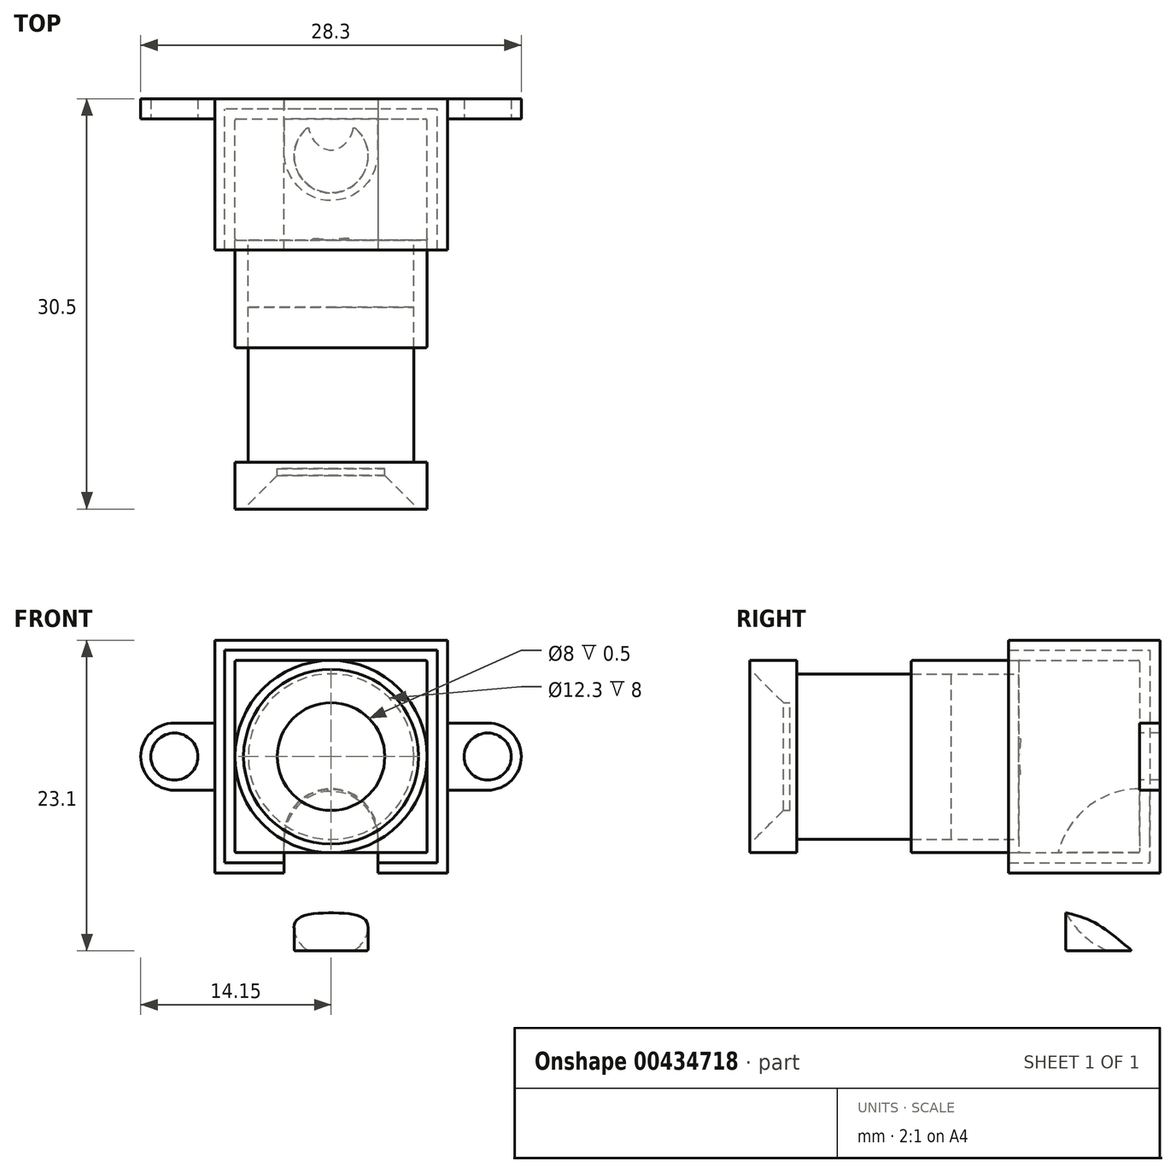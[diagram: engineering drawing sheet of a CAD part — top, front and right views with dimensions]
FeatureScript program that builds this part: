
annotation { "Feature Type Name" : "Feature", "Feature Type Description" : "" }
export const myFeature = defineFeature(function(context is Context, id is Id, definition is map)
    precondition{}
    {
        {
            var Q0;
            Q0=qCreatedBy(makeId("Front.planeOp"),FACE);
            var sketch = newSketch(context, id + "F0", { "sketchPlane" : qUnion([Q0])});
            skLineSegment(sketch, "E0.bottom", {"start": v(-7.15, 7.15) * mm, "end": v(7.15, 7.15) * mm});
            skLineSegment(sketch, "E0.top", {"start": v(-7.15, -7.15) * mm, "end": v(7.15, -7.15) * mm});
            skLineSegment(sketch, "E0.left", {"start": v(-7.15, 7.15) * mm, "end": v(-7.15, -7.15) * mm});
            skLineSegment(sketch, "E0.right", {"start": v(7.15, 7.15) * mm, "end": v(7.15, -7.15) * mm});
            skCircle(sketch, "E1", {"center": v(0, 0) * mm, "radius": 7.15 * mm});
            skCircle(sketch, "E2.0", {"center": v(0, 0) * mm, "radius": 6.15 * mm});
            skSolve(sketch);
        }
        {
            var Q0;
            Q0=qSketchRegion(id+"F0",true);
            var Q1;
            Q1=makeQuery(id+"F0.imprint","IMPRINT",FACE,{"disambiguationData":[TD([[makeQuery(id+"F0.imprint","IMPRINT",EDGE,{"derivedFrom":sQuery(id+"F0.wireOp",EDGE,"E2.0")}),1.0]])]});
            extrude(context, id + "F1", {"entities" : qUnion([Q0, Q1]), "depth" : 9 * mm});
        }
        {
            var Q0;
            Q0=makeQuery(id+"F0.imprint","IMPRINT",FACE,{"disambiguationData":[TD([[makeQuery(id+"F0.imprint","IMPRINT",EDGE,{"derivedFrom":sQuery(id+"F0.wireOp",EDGE,"E2.0")}),-1.0]])]});
            extrude(context, id + "F2", {"entities" : qUnion([Q0]), "operationType" : NewBodyOperationType.ADD, "depth" : 17 * mm});
        }
        {
            var Q0;
            Q0=makeQuery(id+"F2.opExtrude","CAP_FACE",FACE,{"disambiguationData":[OSD([sQuery(id+"F0.wireOp",EDGE,"E1"),sQuery(id+"F0.wireOp",EDGE,"E2.0")])],"isStart":false});
            cPlane(context, id + "F3", {"entities" : qUnion([Q0]), "cplaneType" : CPlaneType.OFFSET, "offset" : 3 * mm, "oppositeDirection" : true, "width" : 150 * mm, "height" : 150 * mm});
        }
        {
            var Q0;
            Q0=qCreatedBy(id+"F3.planeOp",FACE);
            var sketch = newSketch(context, id + "F4", { "sketchPlane" : qUnion([Q0])});
            skCircle(sketch, "E3.0", {"center": v(0, 0) * mm, "radius": 7.15 * mm});
            skCircle(sketch, "E3.1", {"center": v(0, 0) * mm, "radius": 6.15 * mm});
            skCircle(sketch, "E4", {"center": v(0, 0) * mm, "radius": 4 * mm});
            skSolve(sketch);
        }
        {
            var Q0;
            Q0=makeQuery(id+"F4.imprint","IMPRINT",FACE,{"disambiguationData":[TD([[makeQuery(id+"F4.imprint","IMPRINT",EDGE,{"derivedFrom":sQuery(id+"F4.wireOp",EDGE,"E3.1")}),1.0]])]});
            var Q1;
            Q1=makeQuery(id+"F4.imprint","IMPRINT",FACE,{"disambiguationData":[TD([[makeQuery(id+"F4.imprint","IMPRINT",EDGE,{"derivedFrom":sQuery(id+"F4.wireOp",EDGE,"E4")}),1.0]])]});
            extrude(context, id + "F5", {"entities" : qUnion([Q0, Q1]), "depth" : 12 * mm});
        }
        {
            var Q0;
            Q0=makeQuery(id+"F4.imprint","IMPRINT",FACE,{"disambiguationData":[TD([[makeQuery(id+"F4.imprint","IMPRINT",EDGE,{"derivedFrom":sQuery(id+"F4.wireOp",EDGE,"E3.0")}),1.0]])]});
            var Q1;
            Q1=makeQuery(id+"F4.imprint","IMPRINT",FACE,{"disambiguationData":[TD([[makeQuery(id+"F4.imprint","IMPRINT",EDGE,{"derivedFrom":sQuery(id+"F4.wireOp",EDGE,"E3.1")}),1.0]])]});
            extrude(context, id + "F6", {"entities" : qUnion([Q0, Q1]), "operationType" : NewBodyOperationType.ADD, "depth" : 15 * mm, "hasSecondDirection" : true, "secondDirectionOppositeDirection" : false, "secondDirectionDepth" : 11.5 * mm});
        }
        {
            var Q0;
            Q0=makeQuery(id+"F6.opExtrude","CAP_EDGE",EDGE,{"disambiguationData":[OSD([sQuery(id+"F4.wireOp",EDGE,"E4")])],"isStart":false});
            chamfer(context, id + "F7", {"entities" : qUnion([Q0]), "chamferType" : ChamferType.TWO_OFFSETS, "width1" : 2.5 * mm, "oppositeDirection" : false, "width2" : 2.5 * mm, "tangentPropagation" : true});
        }
        {
            var Q0;
            Q0=qCreatedBy(makeId("Top.planeOp"),FACE);
            var sketch = newSketch(context, id + "F8", { "sketchPlane" : qUnion([Q0])});
            skLineSegment(sketch, "E5.0", {"start": v(-7.15, 0) * mm, "end": v(7.15, 0) * mm, "construction": true});
            skCircle(sketch, "E6", {"center": v(0, -2.75) * mm, "radius": 2.75 * mm});
            skSolve(sketch);
        }
        {
            var Q0;
            Q0=makeQuery(id+"F8.imprint","IMPRINT",FACE,{"disambiguationData":[TD([[makeQuery(id+"F8.imprint","IMPRINT",EDGE,{"derivedFrom":sQuery(id+"F8.wireOp",EDGE,"E6")}),1.0]])]});
            extrude(context, id + "F9", {"entities" : qUnion([Q0]), "operationType" : NewBodyOperationType.ADD, "oppositeDirection" : true, "depth" : (21.7 - (14.5 / 2)) * mm});
        }
        {
            var Q0;
            Q0=makeQuery(id+"F1.opExtrude","SWEPT_EDGE",EDGE,{"disambiguationData":[OSD([sQuery(id+"F0.wireOp",EDGE,"E0.top"),sQuery(id+"F0.wireOp",EDGE,"E0.right")])]});
            var Q1;
            Q1=makeQuery(id+"F1.opExtrude","SWEPT_EDGE",EDGE,{"disambiguationData":[OSD([sQuery(id+"F0.wireOp",EDGE,"E0.top"),sQuery(id+"F0.wireOp",EDGE,"E0.left")])]});
            var Q2;
            Q2=makeQuery(id+"F1.opExtrude","SWEPT_EDGE",EDGE,{"disambiguationData":[OSD([sQuery(id+"F0.wireOp",EDGE,"E0.bottom"),sQuery(id+"F0.wireOp",EDGE,"E0.left")])]});
            var Q3;
            Q3=makeQuery(id+"F1.opExtrude","SWEPT_EDGE",EDGE,{"disambiguationData":[OSD([sQuery(id+"F0.wireOp",EDGE,"E0.bottom"),sQuery(id+"F0.wireOp",EDGE,"E0.right")])]});
            var Q4;
            Q4=makeQuery(id+"F2.opExtrude","CAP_EDGE",EDGE,{"disambiguationData":[OSD([sQuery(id+"F0.wireOp",EDGE,"E1")])],"isStart":false});
            var Q5;
            Q5=makeQuery(id+"F1.opExtrude","CAP_EDGE",EDGE,{"disambiguationData":[OSD([sQuery(id+"F0.wireOp",EDGE,"E0.left")])],"isStart":true});
            var Q6;
            {var subQ0=sQuery(id+"F0.wireOp",EDGE,"E0.left");var subQ1=sQuery(id+"F0.wireOp",EDGE,"E0.top");Q6=makeQuery(id+"F9.boolean.opBoolean","SPLIT",EDGE,{"disambiguationData":[TD([makeQuery(id+"F1.opExtrude","SWEPT_FACE",FACE,{"disambiguationData":[OSD([subQ0])]})])],"derivedFrom":makeQuery(id+"F1.opExtrude","CAP_EDGE",EDGE,{"disambiguationData":[OSD([subQ1])],"isStart":true})});}
            var Q7;
            {var subQ0=sQuery(id+"F0.wireOp",EDGE,"E0.right");var subQ1=sQuery(id+"F0.wireOp",EDGE,"E0.top");Q7=makeQuery(id+"F9.boolean.opBoolean","SPLIT",EDGE,{"disambiguationData":[TD([makeQuery(id+"F1.opExtrude","SWEPT_FACE",FACE,{"disambiguationData":[OSD([subQ0])]})])],"derivedFrom":makeQuery(id+"F1.opExtrude","CAP_EDGE",EDGE,{"disambiguationData":[OSD([subQ1])],"isStart":true})});}
            var Q8;
            Q8=makeQuery(id+"F1.opExtrude","CAP_EDGE",EDGE,{"disambiguationData":[OSD([sQuery(id+"F0.wireOp",EDGE,"E0.right")])],"isStart":true});
            var Q9;
            Q9=makeQuery(id+"F1.opExtrude","CAP_EDGE",EDGE,{"disambiguationData":[OSD([sQuery(id+"F0.wireOp",EDGE,"E0.bottom")])],"isStart":true});
            var Q10;
            Q10=makeQuery(id+"F9.opExtrude","CAP_EDGE",EDGE,{"disambiguationData":[OSD([sQuery(id+"F8.wireOp",EDGE,"E6")])],"isStart":false});
            var Q11;
            Q11=makeQuery(id+"F1.opExtrude","SWEPT_FACE",FACE,{"disambiguationData":[OSD([sQuery(id+"F0.wireOp",EDGE,"E0.bottom")])]});
            var Q12;
            Q12=makeQuery(id+"F1.opExtrude","SWEPT_FACE",FACE,{"disambiguationData":[OSD([sQuery(id+"F0.wireOp",EDGE,"E0.left")])]});
            var Q13;
            Q13=makeQuery(id+"F1.opExtrude","SWEPT_FACE",FACE,{"disambiguationData":[OSD([sQuery(id+"F0.wireOp",EDGE,"E0.right")])]});
            var Q14;
            {var subQ0=sQuery(id+"F0.wireOp",EDGE,"E0.right");var subQ1=sQuery(id+"F0.wireOp",EDGE,"E0.top");Q14=makeQuery(id+"F2.boolean.opBoolean","SPLIT",EDGE,{"disambiguationData":[TD([makeQuery(id+"F1.opExtrude","SWEPT_FACE",FACE,{"disambiguationData":[OSD([subQ0])]})])],"derivedFrom":makeQuery(id+"F1.opExtrude","CAP_EDGE",EDGE,{"disambiguationData":[OSD([subQ1])],"isStart":false})});}
            var Q15;
            {var subQ0=sQuery(id+"F0.wireOp",EDGE,"E0.left");var subQ1=sQuery(id+"F0.wireOp",EDGE,"E0.top");Q15=makeQuery(id+"F2.boolean.opBoolean","SPLIT",EDGE,{"disambiguationData":[TD([makeQuery(id+"F1.opExtrude","SWEPT_FACE",FACE,{"disambiguationData":[OSD([subQ0])]})])],"derivedFrom":makeQuery(id+"F1.opExtrude","CAP_EDGE",EDGE,{"disambiguationData":[OSD([subQ1])],"isStart":false})});}
            fillet(context, id + "F10", {"entities" : qUnion([Q0, Q1, Q2, Q3, Q4, Q5, Q6, Q7, Q8, Q9, Q10, Q11, Q12, Q13, Q14, Q15]), "radius" : 0.12 * mm, "tangentPropagation" : true, "allowEdgeOverflow" : false});
        }
        {
            assignVariable(context, id + "F11", {"name" : "Tolerance", "anyValue" : 0.75});
        }
        {
            var Q0;
            Q0=makeQuery(id+"F1.opExtrude","CAP_FACE",FACE,{"disambiguationData":[OSD([sQuery(id+"F0.wireOp",EDGE,"E0.bottom"),sQuery(id+"F0.wireOp",EDGE,"E0.top"),sQuery(id+"F0.wireOp",EDGE,"E0.left"),sQuery(id+"F0.wireOp",EDGE,"E0.right")])],"isStart":true});
            cPlane(context, id + "F12", {"entities" : qUnion([Q0]), "cplaneType" : CPlaneType.OFFSET, "offset" : (getVariable(context, 'Tolerance')) * mm, "width" : 150 * mm, "height" : 150 * mm});
        }
        {
            var Q0;
            Q0=qCreatedBy(id+"F12.planeOp",FACE);
            var sketch = newSketch(context, id + "F13", { "sketchPlane" : qUnion([Q0])});
            skLineSegment(sketch, "E7.0", {"start": v(-7.03, 7.15) * mm, "end": v(7.03, 7.15) * mm, "construction": true});
            skLineSegment(sketch, "E7.1", {"start": v(-7.15, -7.03) * mm, "end": v(-7.15, 7.03) * mm, "construction": true});
            skLineSegment(sketch, "E7.2", {"start": v(7.15, 7.03) * mm, "end": v(7.15, -7.03) * mm, "construction": true});
            skLineSegment(sketch, "E7.3", {"start": v(7.03, -7.15) * mm, "end": v(0.82, -7.15) * mm, "construction": true});
            skLineSegment(sketch, "E7.4", {"start": v(-0.82, -7.15) * mm, "end": v(-7.03, -7.15) * mm, "construction": true});
            skLineSegment(sketch, "E7.5", {"start": v(-0.82, -7.15) * mm, "end": v(0, -7.15) * mm, "construction": true});
            skLineSegment(sketch, "E7.6", {"start": v(0, -7.15) * mm, "end": v(0.82, -7.15) * mm, "construction": true});
            skLineSegment(sketch, "E8.bottom", {"start": v(-7.9, 7.9) * mm, "end": v(7.9, 7.9) * mm});
            skLineSegment(sketch, "E8.top", {"start": v(-7.9, -7.9) * mm, "end": v(7.9, -7.9) * mm});
            skLineSegment(sketch, "E8.left", {"start": v(-7.9, 7.9) * mm, "end": v(-7.9, -7.9) * mm});
            skLineSegment(sketch, "E8.right", {"start": v(7.9, 7.9) * mm, "end": v(7.9, -7.9) * mm});
            skLineSegment(sketch, "E9.0", {"start": v(-8.65, 8.65) * mm, "end": v(8.65, 8.65) * mm});
            skLineSegment(sketch, "E9.1", {"start": v(-8.65, 8.65) * mm, "end": v(-8.65, -8.65) * mm});
            skLineSegment(sketch, "E9.2", {"start": v(-8.65, -8.65) * mm, "end": v(8.65, -8.65) * mm});
            skLineSegment(sketch, "E9.3", {"start": v(8.65, 8.65) * mm, "end": v(8.65, -8.65) * mm});
            skLineSegment(sketch, "E10", {"start": v(0, 0) * mm, "end": v(-11.65, 0) * mm, "construction": true});
            skLineSegment(sketch, "E11", {"start": v(0, 0) * mm, "end": v(11.65, 0) * mm, "construction": true});
            skPoint(sketch, "E11.endSnap0", {"position": v(8.65, 0) * mm});
            skLineSegment(sketch, "E12", {"start": v(11.65, 2.8) * mm, "end": v(11.65, -3.2) * mm, "construction": true});
            skLineSegment(sketch, "E13", {"start": v(-11.65, 2.8) * mm, "end": v(-11.65, -3.2) * mm, "construction": true});
            skLineSegment(sketch, "E14", {"start": v(0, -4.2) * mm, "end": v(0, 4.16) * mm, "construction": true});
            skCircle(sketch, "E15", {"center": v(-11.65, 0) * mm, "radius": 1.75 * mm});
            skArc(sketch, "E16", {"start": v(-11.65, -2.5) * mm, "mid": v(-14.15, 0) * mm, "end": v(-11.65, 2.5) * mm});
            skLineSegment(sketch, "E17", {"start": v(-11.65, 2.5) * mm, "end": v(-8.65, 2.5) * mm});
            skLineSegment(sketch, "E18", {"start": v(-11.65, -2.5) * mm, "end": v(-8.65, -2.5) * mm});
            skLineSegment(sketch, "E19.MirrorCS", {"start": v(11.65, 2.5) * mm, "end": v(8.65, 2.5) * mm});
            skArc(sketch, "E20.MirrorCS", {"start": v(11.65, -2.5) * mm, "mid": v(14.15, 0) * mm, "end": v(11.65, 2.5) * mm});
            skLineSegment(sketch, "E21.MirrorCS", {"start": v(11.65, -2.5) * mm, "end": v(8.65, -2.5) * mm});
            skCircle(sketch, "E22.MirrorC", {"center": v(11.65, 0) * mm, "radius": 1.75 * mm});
            skSolve(sketch);
        }
        {
            var Q0;
            Q0=makeQuery(id+"F13.imprint","IMPRINT",FACE,{"disambiguationData":[TD([[makeQuery(id+"F13.imprint","IMPRINT",EDGE,{"derivedFrom":sQuery(id+"F13.wireOp",EDGE,"E8.bottom")}),1.0]])]});
            extrude(context, id + "F14", {"entities" : qUnion([Q0]), "oppositeDirection" : true, "depth" : (9 + (getVariable(context, 'Tolerance') * 2)) * mm});
        }
        {
            var Q0;
            Q0=makeQuery(id+"F13.imprint","IMPRINT",FACE,{"disambiguationData":[TD([[makeQuery(id+"F13.imprint","IMPRINT",EDGE,{"derivedFrom":sQuery(id+"F13.wireOp",EDGE,"E8.bottom")}),-1.0]])]});
            var Q1;
            Q1=makeQuery(id+"F13.imprint","IMPRINT",FACE,{"disambiguationData":[TD([[makeQuery(id+"F13.imprint","IMPRINT",EDGE,{"derivedFrom":sQuery(id+"F13.wireOp",EDGE,"E8.bottom")}),1.0]])]});
            extrude(context, id + "F15", {"entities" : qUnion([Q0, Q1]), "operationType" : NewBodyOperationType.ADD, "depth" : 0.75 * mm});
        }
        {
            var Q0;
            Q0=makeQuery(id+"F13.imprint","IMPRINT",FACE,{"disambiguationData":[TD([[makeQuery(id+"F13.imprint","IMPRINT",EDGE,{"derivedFrom":sQuery(id+"F13.wireOp",EDGE,"E15")}),-1.0]])]});
            var Q1;
            {var subQ1=sQuery(id+"F13.wireOp",EDGE,"E19.MirrorCS");Q1=makeQuery(id+"F13.imprint","IMPRINT",FACE,{"disambiguationData":[TD([[makeQuery(id+"F13.imprint","IMPRINT",EDGE,{"derivedFrom":subQ1}),1.0]])]});}
            extrude(context, id + "F16", {"entities" : qUnion([Q0, Q1]), "operationType" : NewBodyOperationType.ADD, "depth" : 1.5 * mm, "symmetric" : true});
        }
        {
            var Q0;
            Q0=qCreatedBy(makeId("Front.planeOp"),FACE);
            var sketch = newSketch(context, id + "F17", { "sketchPlane" : qUnion([Q0])});
            skLineSegment(sketch, "E23", {"start": v(0, -5.7) * mm, "end": v(0, 1.63) * mm, "construction": true});
            skCircle(sketch, "E24.0", {"center": v(0, -11.4) * mm, "radius": 2.75 * mm, "construction": true});
            skArc(sketch, "E25", {"start": v(-3.5, -11.4) * mm, "mid": v(0, -14.9) * mm, "end": v(3.5, -11.4) * mm});
            skLineSegment(sketch, "E26", {"start": v(-3.5, -11.4) * mm, "end": v(-3.5, -8.65) * mm});
            skLineSegment(sketch, "E27", {"start": v(-3.5, -8.65) * mm, "end": v(3.5, -8.65) * mm});
            skLineSegment(sketch, "E28", {"start": v(3.5, -8.65) * mm, "end": v(3.5, -11.4) * mm});
            skLineSegment(sketch, "E29.0", {"start": v(8.65, -8.65) * mm, "end": v(-8.65, -8.65) * mm, "construction": true});
            skSolve(sketch);
        }
        {
            var Q0;
            Q0=qSketchRegion(id+"F17",true);
            var Q1;
            Q1=sQuery(id+"F17.wireOp",EDGE,"E27");
            revolve(context, id + "F18", {"operationType" : NewBodyOperationType.REMOVE, "entities" : qUnion([Q0]), "axis" : qUnion([Q1]), "revolveType" : RevolveType.FULL, "oppositeDirection" : true});
        }
        {
            var Q0;
            {var subQ0=sQuery(id+"F13.wireOp",EDGE,"E9.2");Q0=makeQuery(id+"F15.boolean.opBoolean","MERGE",FACE,{"derivedFrom":[makeQuery(id+"F14.opExtrude","SWEPT_FACE",FACE,{"disambiguationData":[OSD([subQ0])]}),makeQuery(id+"F15.opExtrude","SWEPT_FACE",FACE,{"disambiguationData":[OSD([subQ0])]})]});}
            var sketch = newSketch(context, id + "F19", { "sketchPlane" : qUnion([Q0])});
            skLineSegment(sketch, "E30.0", {"start": v(-3.5, 2.75) * mm, "end": v(-3.5, -1.5) * mm});
            skLineSegment(sketch, "E30.1", {"start": v(3.5, -1.5) * mm, "end": v(3.5, 2.75) * mm});
            skLineSegment(sketch, "E31", {"start": v(-3.5, 2.75) * mm, "end": v(-3.5, 9.75) * mm});
            skLineSegment(sketch, "E32", {"start": v(-3.5, 9.75) * mm, "end": v(3.5, 9.75) * mm});
            skPoint(sketch, "E32.endSnap0", {"position": v(0, 9.75) * mm});
            skLineSegment(sketch, "E33", {"start": v(3.5, 9.75) * mm, "end": v(3.5, 2.75) * mm});
            skLineSegment(sketch, "E34", {"start": v(-3.5, 2.75) * mm, "end": v(3.5, 2.75) * mm, "construction": true});
            skLineSegment(sketch, "E35", {"start": v(-3.5, -1.5) * mm, "end": v(3.5, -1.5) * mm});
            skSolve(sketch);
        }
        {
            var Q0;
            Q0=qSketchRegion(id+"F19",true);
            var Q1;
            Q1=makeQuery(id+"F14.opExtrude","SWEPT_FACE",FACE,{"disambiguationData":[OSD([sQuery(id+"F13.wireOp",EDGE,"E8.top")])]});
            extrude(context, id + "F20", {"entities" : qUnion([Q0]), "operationType" : NewBodyOperationType.REMOVE, "oppositeDirection" : true, "endBoundEntityFace" : qUnion([Q1]), "depth" : 1 * mm});
        }
    });
